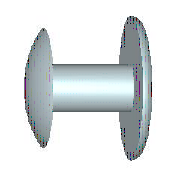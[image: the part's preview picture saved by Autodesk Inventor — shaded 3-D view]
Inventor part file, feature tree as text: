
AUTODESK INVENTOR PART (.ipt)
format: ipt  version: 2019 (Build 230136000, 136)  size: 175,616 bytes
history: native  units: mm
features: revolve x1, sketch x1
ambient origin geometry x8: Origin, YZ Plane, XZ Plane, XY Plane, X Axis, Y Axis, Z Axis, Center Point
bodies: Solid1 (feature_tree)
feature tree (2):
  revolve  "Revolution 1"  Angle=90.0deg
  sketch  "Sketch1"  dims[d15=1.8mm d16=90.0deg d20=5.975952mm d21=0.65mm d22=60.0deg d25=0.65mm d26=0.65mm]
